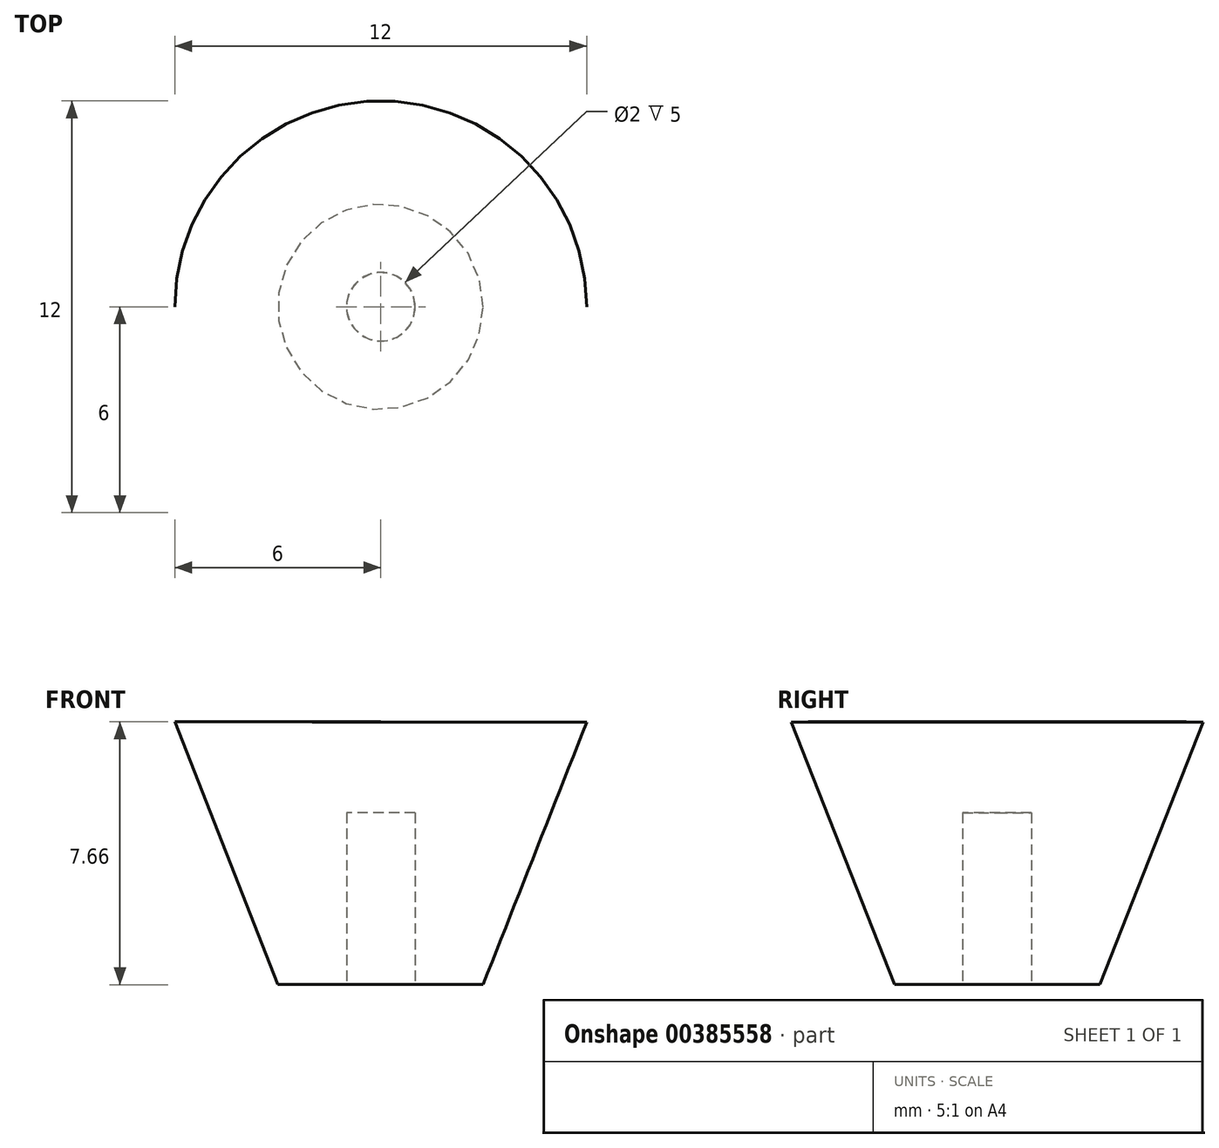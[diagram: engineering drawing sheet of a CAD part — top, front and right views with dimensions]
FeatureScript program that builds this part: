
annotation { "Feature Type Name" : "Feature", "Feature Type Description" : "" }
export const myFeature = defineFeature(function(context is Context, id is Id, definition is map)
    precondition{}
    {
        {
            var Q0;
            Q0=qCreatedBy(makeId("Front.planeOp"),FACE);
            var sketch = newSketch(context, id + "F0", { "sketchPlane" : qUnion([Q0])});
            skLineSegment(sketch, "E0", {"start": v(0, 0) * mm, "end": v(-3, 0) * mm});
            skLineSegment(sketch, "E1", {"start": v(-3, 0) * mm, "end": v(-6, 7.65) * mm});
            skLineSegment(sketch, "E2", {"start": v(-6, 7.65) * mm, "end": v(0, 7.65) * mm});
            skLineSegment(sketch, "E3", {"start": v(0, 7.65) * mm, "end": v(-0.02, -7.35) * mm});
            skSolve(sketch);
        }
        {
            var Q0;
            Q0 = qSketchRegion(id + "F0", true);
            var Q1;
            Q1=sQuery(id+"F0.wireOp",EDGE,"E3");
            revolve(context, id + "F1", {"entities" : qUnion([Q0]), "axis" : qUnion([Q1]), "revolveType" : RevolveType.FULL});
        }
        {
            var Q0;
            Q0=qCreatedBy(makeId("Top.planeOp"),FACE);
            var sketch = newSketch(context, id + "F2", { "sketchPlane" : qUnion([Q0])});
            skCircle(sketch, "E4", {"center": v(0, 0) * mm, "radius": 1 * mm});
            skSolve(sketch);
        }
        {
            var Q0;
            Q0 = qSketchRegion(id + "F2", true);
            extrude(context, id + "F3", {"entities" : qUnion([Q0]), "operationType" : NewBodyOperationType.REMOVE, "depth" : 5 * mm});
        }
    });
